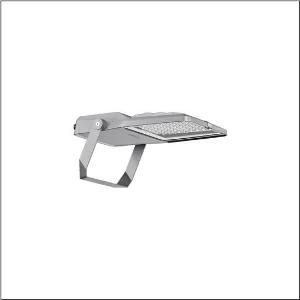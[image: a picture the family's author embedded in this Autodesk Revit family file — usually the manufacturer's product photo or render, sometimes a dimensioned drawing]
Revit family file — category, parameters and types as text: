
# Revit family: floodlight_fl_21_iq_mini___pl33t_5xa7771b2f1a_e875
name_source: partatom
category: Lighting Fixtures
units: mm (PartAtom-declared; Revit-internal decimal feet)

## family parameters
Cut with Voids When Loaded = No
Host = Face
Light Source = No
Part Type = Normal
Room Calculation Point = No
Round Connector Dimension = Use Diameter
Shared = No

## types (1)
- --- (1 x LED, 6170 lm, 45.5 W, 3000K)
    Apparent Load = 46 VA
    CIE Flux Codes = 26 75 99 100 100
    Color Rendering = 70
    Color Temperature = 3000K
    Default Elevation = 1800 mm
    Description = Floodlight FL 21 iQ mini, floodlight, primary light control with lens, of PMMA, primary optical cover: protective disc, of toughened safety glass, transparent, light distribution: PL33T, light emission: direct distribution, installation type: surface-mounted, lamps: LED, High Power LED, rated values: 6.170lm | 45,5W | 135,6lm/W (begin service life); end service life: 6.170lm | 48W; at 50% lumin. flux: 3.085lm | 21,5W | 143,5lm/W, colour temperature: 3000K, colour rendering: CRI > 70, light colour: 730, light setting 1 begin service life: 100% | 6.170lm | 45,5W | 135,6lm/W | 3.000K, light setting 1 end service life: 48W, further light settings possible, control: Auto-Match, Temp-Guard, Lumen-Switch, Night-Set, Smart-Wire, Light-Fading, Desk-Remote (wireless, voltage-free reading and setting of iQ features in the workshop via application-optimized NFC function/RFID function), optimised constant luminous flux control (CLO 2.0), pre-setting: linear dimming characteristic, with terminal, 6-pole, mains connection: 220..240V, AC, 50/60Hz, luminaire housing, of diecast aluminium, powder-coated, SITECO metallic grey (DB 702S), corrosivity category C5 mid according to DIN EN ISO 12944suitable for swimming poolschlorine-resistant, sealing non-destructively replaceable, mounting bracket, of steel, galvanised, powder-coated, SITECO metallic grey (DB 702S), protection rating (complete): IP66, insulation class (complete): insulation class II (safety insulation), certification: CE, ENEC, VDE, protection symbol: D, impact resistance: IK08, permissible operating ambient temperature: -40..+40°C, permissible operating ambient temperature for outdoor applications: -40..+50°C, standard: DIN EN 12944, LABS conformity tested according to VDMA 24364:2018-05, packaging unit: 1 piece

Light Distribution: PL33T
    Height = 70 mm
    Lamp = 1 x LED
    Lamp Light Flux = 6170 lm
    Lamp Power = 45.5 W
    Lamp count = 1
    Length = 485 mm
    Luminous efficacy = 136 lm/W
    Manufacturer = Siteco
    ModVariant = No
    Model = 5XA7771B2F1A
    Mounting Place = Wall
    Mounting Type = Surface mounted
    Number of Poles = 1
    OnlyDefault = Yes
    Power Factor = 1
    Product Name = Floodlight FL 21 iQ mini | PL33T
    Product group = floodlight | wall mounted
    ProductGroupID = 2002
    Protection Class = Protection class II
    Protection Degree = IP 66
    RLX_Detail_Level = 1
    RLX_Emergency_Light_Flux = 0 lm
    RLX_Emergency_Type = 0
    RLX_Emergency_Type_DB = No
    RlxData = <blob elided: 96297 chars, md5=d67fd49f>
    Socket = socket
    Standby Power = 0 W
    System Light Flux = 6170 lm
    System Power = 46 W
    Type Comments = factory setting: luminous flux: 100 % | dim-lin: 254 | 463 mA
    Type Image = l_1006845.jpg
    URL = http://relux.com
    VarID = @adj_151407
    Voltage = 0 V
    Weight = 0.00 kg
    Width = 337 mm

## geometry (parser evidence)
native form markers: Blend x4, Sweep x12
no freeform markers — native parametric forms only
